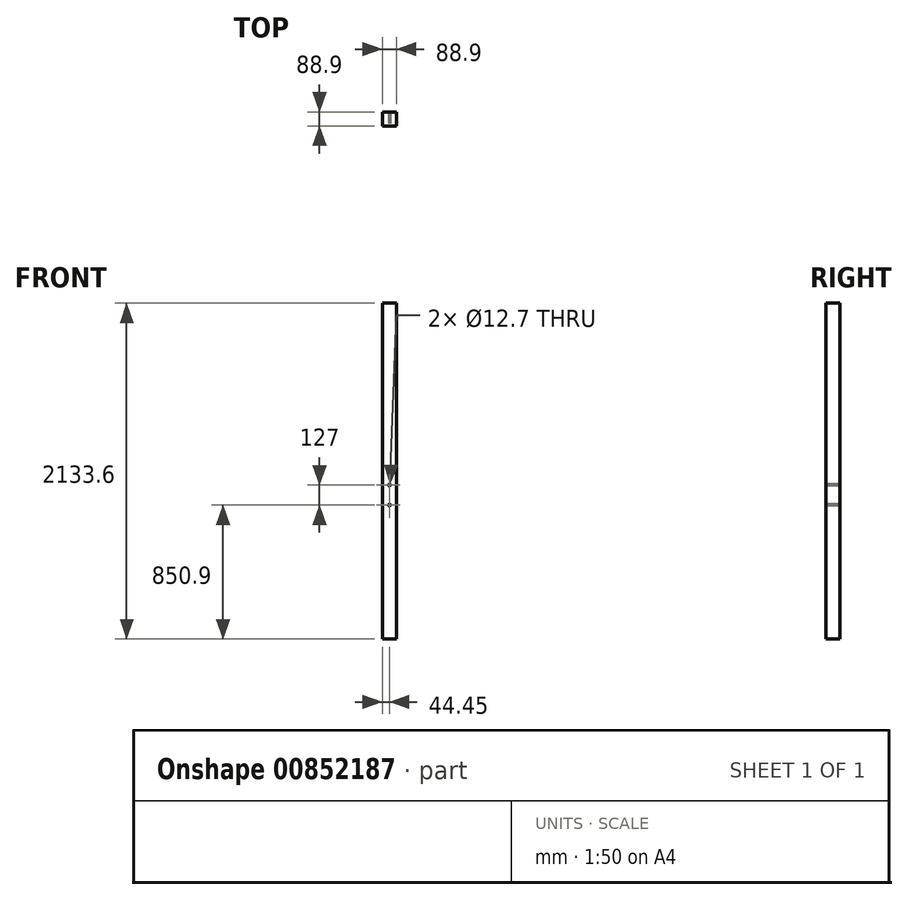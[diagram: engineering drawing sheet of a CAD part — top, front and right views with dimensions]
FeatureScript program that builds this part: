
annotation { "Feature Type Name" : "Feature", "Feature Type Description" : "" }
export const myFeature = defineFeature(function(context is Context, id is Id, definition is map)
    precondition{}
    {
        {
            var Q0;
            Q0=qCreatedBy(makeId("Top.planeOp"),FACE);
            var sketch = newSketch(context, id + "F0", { "sketchPlane" : qUnion([Q0])});
            skLineSegment(sketch, "E0.bottom", {"start": v(44.45, -44.45) * mm, "end": v(-44.45, -44.45) * mm});
            skLineSegment(sketch, "E0.top", {"start": v(44.45, 44.45) * mm, "end": v(-44.45, 44.45) * mm});
            skLineSegment(sketch, "E0.left", {"start": v(44.45, -44.45) * mm, "end": v(44.45, 44.45) * mm});
            skLineSegment(sketch, "E0.right", {"start": v(-44.45, -44.45) * mm, "end": v(-44.45, 44.45) * mm});
            skPoint(sketch, "E0.middle", {"position": v(0, 0) * mm});
            skSolve(sketch);
        }
        {
            var Q0;
            Q0 = qSketchRegion(id + "F0", true);
            extrude(context, id + "F1", {"entities" : qUnion([Q0]), "endBound" : BoundingType.SYMMETRIC, "depth" : 2133.6 * mm, "offsetDistance" : 25.4 * mm});
        }
        {
            var Q0;
            Q0=qCreatedBy(makeId("Front.planeOp"),FACE);
            var sketch = newSketch(context, id + "F2", { "sketchPlane" : qUnion([Q0])});
            skLineSegment(sketch, "E1", {"start": v(0, 0) * mm, "end": v(0, -152.4) * mm, "construction": true});
            skLineSegment(sketch, "E2", {"start": v(0, -88.9) * mm, "end": v(0, -215.9) * mm, "construction": true});
            skCircle(sketch, "E3", {"center": v(0, -88.9) * mm, "radius": 6.35 * mm});
            skCircle(sketch, "E4", {"center": v(0, -215.9) * mm, "radius": 6.35 * mm});
            skSolve(sketch);
        }
        {
            var Q0;
            Q0 = qSketchRegion(id + "F2", true);
            extrude(context, id + "F3", {"entities" : qUnion([Q0]), "operationType" : NewBodyOperationType.REMOVE, "endBound" : BoundingType.SYMMETRIC, "oppositeDirection" : true, "depth" : 101.6 * mm, "offsetDistance" : 25.4 * mm});
        }
    });
